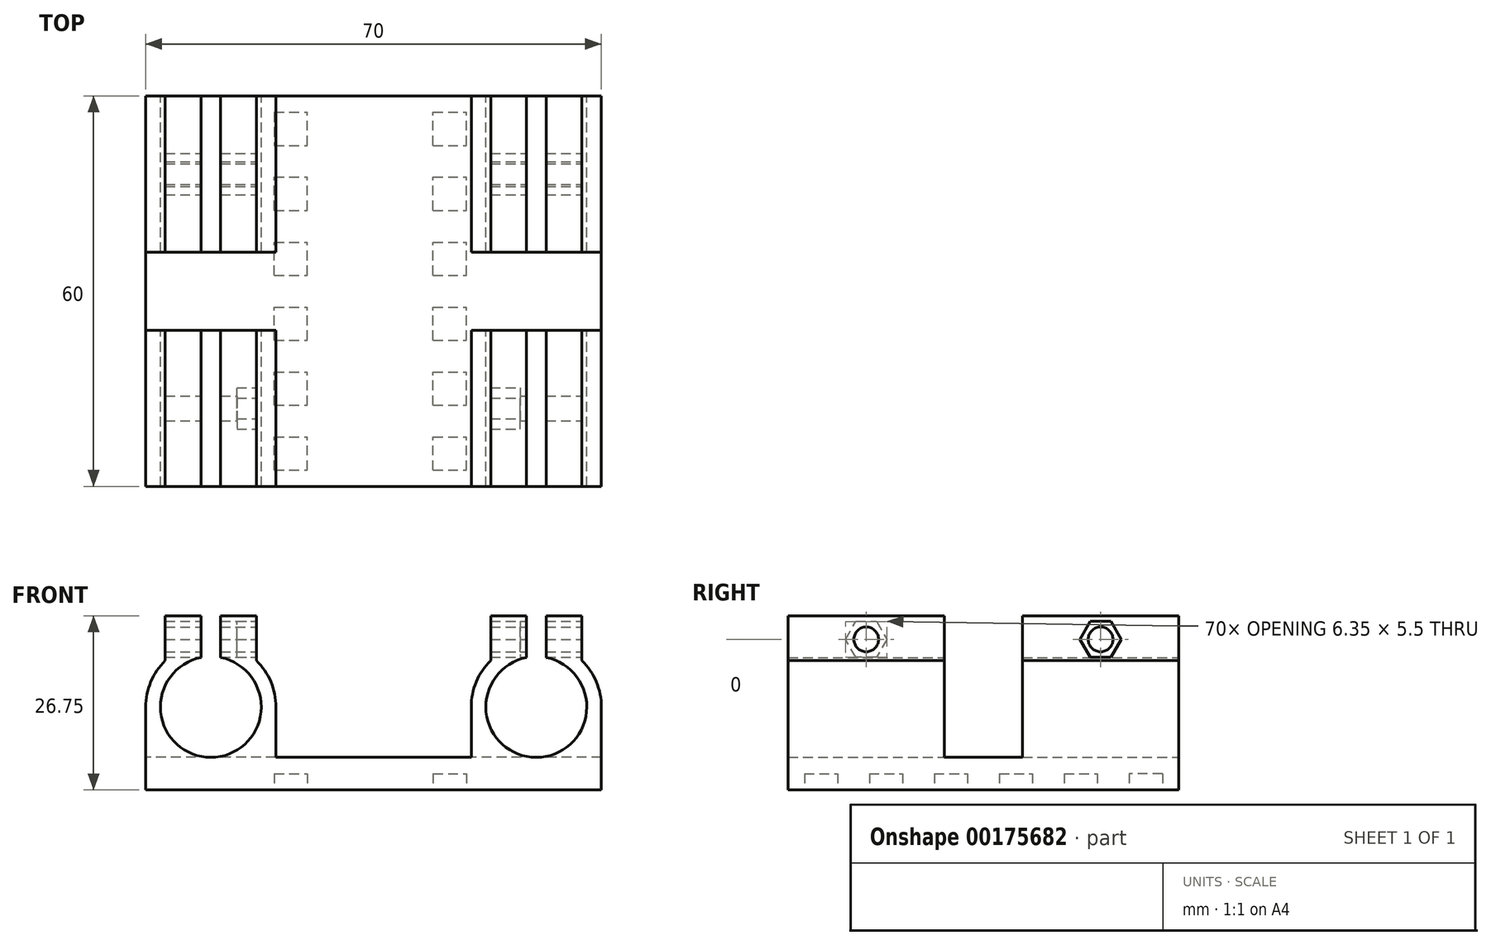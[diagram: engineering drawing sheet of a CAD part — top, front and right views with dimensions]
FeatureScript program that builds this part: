
annotation { "Feature Type Name" : "Feature", "Feature Type Description" : "" }
export const myFeature = defineFeature(function(context is Context, id is Id, definition is map)
    precondition{}
    {
        {
            var Q0;
            Q0=qCreatedBy(makeId("Front.planeOp"),FACE);
            var sketch = newSketch(context, id + "F0", { "sketchPlane" : qUnion([Q0])});
            skLineSegment(sketch, "E0", {"start": v(0, 0) * mm, "end": v(-35, 0) * mm});
            skLineSegment(sketch, "E1", {"start": v(-35, 0) * mm, "end": v(-35, 12.75) * mm});
            skLineSegment(sketch, "E2", {"start": v(-15, 12.75) * mm, "end": v(-15, 5) * mm});
            skLineSegment(sketch, "E3", {"start": v(-15, 5) * mm, "end": v(0, 5) * mm});
            skArc(sketch, "E4", {"start": v(-26.5, 20.35) * mm, "mid": v(-25, 5) * mm, "end": v(-23.5, 20.35) * mm});
            skArc(sketch, "E5", {"start": v(-15, 12.75) * mm, "mid": v(-15.78, 16.62) * mm, "end": v(-18, 19.9) * mm});
            skLineSegment(sketch, "E6", {"start": v(-32, 19.9) * mm, "end": v(-32, 26.75) * mm});
            skLineSegment(sketch, "E7", {"start": v(-32, 26.75) * mm, "end": v(-26.5, 26.75) * mm});
            skLineSegment(sketch, "E8", {"start": v(-18, 26.75) * mm, "end": v(-18, 19.9) * mm});
            skLineSegment(sketch, "E9", {"start": v(-25, 33.97) * mm, "end": v(-25, -14.1) * mm, "construction": true});
            skLineSegment(sketch, "E10", {"start": v(-26.5, 26.75) * mm, "end": v(-26.5, 20.35) * mm});
            skLineSegment(sketch, "E11", {"start": v(-23.5, 26.75) * mm, "end": v(-23.5, 20.35) * mm});
            skLineSegment(sketch, "E12.trimOffspring", {"start": v(-23.5, 26.75) * mm, "end": v(-18, 26.75) * mm});
            skArc(sketch, "E13.trimOffspring", {"start": v(-32, 19.9) * mm, "mid": v(-34.22, 16.62) * mm, "end": v(-35, 12.75) * mm});
            skLineSegment(sketch, "E14.MirrorCS", {"start": v(15, 5) * mm, "end": v(0, 5) * mm});
            skLineSegment(sketch, "E15.MirrorCS", {"start": v(0, 0) * mm, "end": v(35, 0) * mm});
            skLineSegment(sketch, "E16.MirrorCS", {"start": v(35, 0) * mm, "end": v(35, 12.75) * mm});
            skArc(sketch, "E17.MirrorCS", {"start": v(32, 19.9) * mm, "mid": v(34.22, 16.62) * mm, "end": v(35, 12.75) * mm});
            skLineSegment(sketch, "E18.MirrorCS", {"start": v(32, 19.9) * mm, "end": v(32, 26.75) * mm});
            skLineSegment(sketch, "E19.MirrorCS", {"start": v(32, 26.75) * mm, "end": v(26.5, 26.75) * mm});
            skLineSegment(sketch, "E20.MirrorCS", {"start": v(26.5, 26.75) * mm, "end": v(26.5, 20.35) * mm});
            skArc(sketch, "E21.MirrorCS", {"start": v(26.5, 20.35) * mm, "mid": v(25, 5) * mm, "end": v(23.5, 20.35) * mm});
            skLineSegment(sketch, "E22.MirrorCS", {"start": v(23.5, 26.75) * mm, "end": v(23.5, 20.35) * mm});
            skLineSegment(sketch, "E23.MirrorCS", {"start": v(23.5, 26.75) * mm, "end": v(18, 26.75) * mm});
            skLineSegment(sketch, "E24.MirrorCS", {"start": v(18, 26.75) * mm, "end": v(18, 19.9) * mm});
            skArc(sketch, "E25.MirrorCS", {"start": v(15, 12.75) * mm, "mid": v(15.78, 16.62) * mm, "end": v(18, 19.9) * mm});
            skLineSegment(sketch, "E26.MirrorCS", {"start": v(15, 12.75) * mm, "end": v(15, 5) * mm});
            skSolve(sketch);
        }
        {
            var Q0;
            Q0 = qSketchRegion(id + "F0", true);
            extrude(context, id + "F1", {"entities" : qUnion([Q0]), "endBound" : BoundingType.SYMMETRIC, "depth" : 60 * mm});
        }
        {
            var Q0;
            Q0=makeQuery(id+"F1.opExtrude","SWEPT_FACE",FACE,{"disambiguationData":[OSD([sQuery(id+"F0.wireOp",EDGE,"E26.MirrorCS")])]});
            var sketch = newSketch(context, id + "F2", { "sketchPlane" : qUnion([Q0])});
            skLineSegment(sketch, "E27.0", {"start": v(30, 26.75) * mm, "end": v(-30, 26.75) * mm});
            skLineSegment(sketch, "E28.bottom", {"start": v(-6, 5) * mm, "end": v(6, 5) * mm});
            skLineSegment(sketch, "E28.top", {"start": v(-6, 26.75) * mm, "end": v(6, 26.75) * mm});
            skLineSegment(sketch, "E28.left", {"start": v(-6, 5) * mm, "end": v(-6, 26.75) * mm});
            skLineSegment(sketch, "E28.right", {"start": v(6, 5) * mm, "end": v(6, 26.75) * mm});
            skSolve(sketch);
        }
        {
            var Q0;
            Q0 = qSketchRegion(id + "F2", true);
            extrude(context, id + "F3", {"entities" : qUnion([Q0]), "operationType" : NewBodyOperationType.REMOVE, "endBound" : BoundingType.THROUGH_ALL, "oppositeDirection" : true, "depth" : 25 * mm, "hasSecondDirection" : true, "secondDirectionBound" : SecondDirectionBoundingType.THROUGH_ALL, "secondDirectionOppositeDirection" : false, "secondDirectionDepth" : 25 * mm});
        }
        {
            var Q0;
            {var subQ1=sQuery(id+"F0.wireOp",EDGE,"E8");Q0=makeQuery(id+"F3.boolean.opBoolean","SPLIT",FACE,{"disambiguationData":[TD([makeQuery(id+"F3.opExtrude","SWEPT_FACE",FACE,{"disambiguationData":[OSD([sQuery(id+"F2.wireOp",EDGE,"E28.right")])]})])],"derivedFrom":makeQuery(id+"F1.opExtrude","SWEPT_FACE",FACE,{"disambiguationData":[OSD([subQ1])]})});}
            var sketch = newSketch(context, id + "F4", { "sketchPlane" : qUnion([Q0])});
            skCircle(sketch, "E29.cCircle", {"center": v(-18, 23.14) * mm, "radius": 2.75 * mm, "construction": true});
            skLineSegment(sketch, "E29.0", {"start": v(-14.82, 23.14) * mm, "end": v(-16.41, 20.4) * mm});
            skLineSegment(sketch, "E29.1", {"start": v(-16.41, 20.4) * mm, "end": v(-19.59, 20.4) * mm});
            skLineSegment(sketch, "E29.2", {"start": v(-19.59, 20.4) * mm, "end": v(-21.18, 23.14) * mm});
            skLineSegment(sketch, "E29.3", {"start": v(-21.18, 23.14) * mm, "end": v(-19.59, 25.9) * mm});
            skLineSegment(sketch, "E29.4", {"start": v(-19.59, 25.9) * mm, "end": v(-16.41, 25.9) * mm});
            skLineSegment(sketch, "E29.5", {"start": v(-16.41, 25.9) * mm, "end": v(-14.82, 23.14) * mm});
            skPoint(sketch, "E29.0.midPoint", {"position": v(-15.62, 21.77) * mm});
            skCircle(sketch, "E30.MirrorC", {"center": v(18, 23.14) * mm, "radius": 2.75 * mm, "construction": true});
            skLineSegment(sketch, "E31.MirrorCS", {"start": v(16.41, 25.9) * mm, "end": v(14.82, 23.14) * mm});
            skLineSegment(sketch, "E32.MirrorCS", {"start": v(19.59, 25.9) * mm, "end": v(16.41, 25.9) * mm});
            skLineSegment(sketch, "E33.MirrorCS", {"start": v(21.18, 23.14) * mm, "end": v(19.59, 25.9) * mm});
            skLineSegment(sketch, "E34.MirrorCS", {"start": v(19.59, 20.4) * mm, "end": v(21.18, 23.14) * mm});
            skLineSegment(sketch, "E35.MirrorCS", {"start": v(16.41, 20.4) * mm, "end": v(19.59, 20.4) * mm});
            skLineSegment(sketch, "E36.MirrorCS", {"start": v(14.82, 23.14) * mm, "end": v(16.41, 20.4) * mm});
            skCircle(sketch, "E37", {"center": v(-18, 23.14) * mm, "radius": 1.9 * mm});
            skCircle(sketch, "E38.MirrorC", {"center": v(18, 23.14) * mm, "radius": 1.9 * mm});
            skSolve(sketch);
        }
        {
            var Q0;
            Q0 = qSketchRegion(id + "F4", true);
            extrude(context, id + "F5", {"entities" : qUnion([Q0]), "operationType" : NewBodyOperationType.REMOVE, "oppositeDirection" : true, "depth" : 3 * mm, "hasSecondDirection" : true, "secondDirectionOppositeDirection" : false, "secondDirectionDepth" : 40.5 * mm});
        }
        {
            var Q0;
            Q0=makeQuery(id+"F4.imprint","IMPRINT",FACE,{"disambiguationData":[TD([[makeQuery(id+"F4.imprint","IMPRINT",EDGE,{"derivedFrom":sQuery(id+"F4.wireOp",EDGE,"E38.MirrorC")}),-1.0]])]});
            var Q1;
            Q1=makeQuery(id+"F4.imprint","IMPRINT",FACE,{"disambiguationData":[TD([[makeQuery(id+"F4.imprint","IMPRINT",EDGE,{"derivedFrom":sQuery(id+"F4.wireOp",EDGE,"E37")}),1.0]])]});
            extrude(context, id + "F6", {"entities" : qUnion([Q0, Q1]), "operationType" : NewBodyOperationType.REMOVE, "endBound" : BoundingType.THROUGH_ALL, "oppositeDirection" : true, "depth" : 25 * mm, "hasSecondDirection" : true, "secondDirectionBound" : SecondDirectionBoundingType.THROUGH_ALL, "secondDirectionOppositeDirection" : false, "secondDirectionDepth" : 25 * mm});
        }
        {
            var Q0;
            Q0=makeQuery(id+"F1.opExtrude","SWEPT_FACE",FACE,{"disambiguationData":[OSD([sQuery(id+"F0.wireOp",EDGE,"E0"),sQuery(id+"F0.wireOp",EDGE,"E15.MirrorCS")])]});
            var sketch = newSketch(context, id + "F7", { "sketchPlane" : qUnion([Q0])});
            skLineSegment(sketch, "E39.bottom", {"start": v(-15.25, 27.5) * mm, "end": v(-10.15, 27.5) * mm});
            skLineSegment(sketch, "E39.top", {"start": v(-15.25, 22.4) * mm, "end": v(-10.15, 22.4) * mm});
            skLineSegment(sketch, "E39.left", {"start": v(-15.25, 27.5) * mm, "end": v(-15.25, 22.4) * mm});
            skLineSegment(sketch, "E39.right", {"start": v(-10.15, 27.5) * mm, "end": v(-10.15, 22.4) * mm});
            skLineSegment(sketch, "E40.1.0.0", {"start": v(14.25, 27.5) * mm, "end": v(14.25, 22.4) * mm});
            skLineSegment(sketch, "E40.1.0.1", {"start": v(9.15, 27.5) * mm, "end": v(14.25, 27.5) * mm});
            skLineSegment(sketch, "E40.1.0.2", {"start": v(9.15, 27.5) * mm, "end": v(9.15, 22.4) * mm});
            skLineSegment(sketch, "E40.1.0.3", {"start": v(9.15, 22.4) * mm, "end": v(14.25, 22.4) * mm});
            skLineSegment(sketch, "E40.direction1", {"start": v(-10.15, 22.4) * mm, "end": v(14.25, 22.4) * mm, "construction": true});
            skLineSegment(sketch, "E41.1.0.0", {"start": v(-10.15, 17.52) * mm, "end": v(-10.15, 12.42) * mm});
            skLineSegment(sketch, "E41.1.0.1", {"start": v(-15.25, 17.52) * mm, "end": v(-15.25, 12.42) * mm});
            skLineSegment(sketch, "E41.1.0.2", {"start": v(-15.25, 12.42) * mm, "end": v(-10.15, 12.42) * mm});
            skLineSegment(sketch, "E41.1.0.3", {"start": v(-15.25, 17.52) * mm, "end": v(-10.15, 17.52) * mm});
            skLineSegment(sketch, "E41.1.0.4", {"start": v(9.15, 17.52) * mm, "end": v(14.25, 17.52) * mm});
            skLineSegment(sketch, "E41.1.0.5", {"start": v(9.15, 17.52) * mm, "end": v(9.15, 12.42) * mm});
            skLineSegment(sketch, "E41.1.0.6", {"start": v(14.25, 17.52) * mm, "end": v(14.25, 12.42) * mm});
            skLineSegment(sketch, "E41.1.0.7", {"start": v(-10.15, 12.42) * mm, "end": v(14.25, 12.42) * mm, "construction": true});
            skLineSegment(sketch, "E41.2.0.0", {"start": v(-10.15, 7.54) * mm, "end": v(-10.15, 2.44) * mm});
            skLineSegment(sketch, "E41.2.0.1", {"start": v(-15.25, 7.54) * mm, "end": v(-15.25, 2.44) * mm});
            skLineSegment(sketch, "E41.2.0.2", {"start": v(-15.25, 2.44) * mm, "end": v(-10.15, 2.44) * mm});
            skLineSegment(sketch, "E41.2.0.3", {"start": v(-15.25, 7.54) * mm, "end": v(-10.15, 7.54) * mm});
            skLineSegment(sketch, "E41.2.0.4", {"start": v(9.15, 7.54) * mm, "end": v(14.25, 7.54) * mm});
            skLineSegment(sketch, "E41.2.0.5", {"start": v(9.15, 7.54) * mm, "end": v(9.15, 2.44) * mm});
            skLineSegment(sketch, "E41.2.0.6", {"start": v(14.25, 7.54) * mm, "end": v(14.25, 2.44) * mm});
            skLineSegment(sketch, "E41.2.0.7", {"start": v(-10.15, 2.44) * mm, "end": v(14.25, 2.44) * mm, "construction": true});
            skLineSegment(sketch, "E41.direction1", {"start": v(-10.15, 22.4) * mm, "end": v(-10.15, 12.42) * mm, "construction": true});
            skLineSegment(sketch, "E42.0.3.0", {"start": v(-10.15, -2.44) * mm, "end": v(-10.15, -7.54) * mm});
            skLineSegment(sketch, "E42.3.3.0", {"start": v(-15.25, -2.44) * mm, "end": v(-15.25, -7.54) * mm});
            skLineSegment(sketch, "E42.6.3.0", {"start": v(-15.25, -7.54) * mm, "end": v(-10.15, -7.54) * mm});
            skLineSegment(sketch, "E42.9.3.0", {"start": v(-15.25, -2.44) * mm, "end": v(-10.15, -2.44) * mm});
            skLineSegment(sketch, "E42.12.3.0", {"start": v(9.15, -2.44) * mm, "end": v(14.25, -2.44) * mm});
            skLineSegment(sketch, "E42.15.3.0", {"start": v(9.15, -2.44) * mm, "end": v(9.15, -7.54) * mm});
            skLineSegment(sketch, "E42.18.3.0", {"start": v(14.25, -2.44) * mm, "end": v(14.25, -7.54) * mm});
            skLineSegment(sketch, "E42.21.3.0", {"start": v(-10.15, -7.54) * mm, "end": v(14.25, -7.54) * mm, "construction": true});
            skLineSegment(sketch, "E42.0.4.0", {"start": v(-10.15, -12.42) * mm, "end": v(-10.15, -17.52) * mm});
            skLineSegment(sketch, "E42.3.4.0", {"start": v(-15.25, -12.42) * mm, "end": v(-15.25, -17.52) * mm});
            skLineSegment(sketch, "E42.6.4.0", {"start": v(-15.25, -17.52) * mm, "end": v(-10.15, -17.52) * mm});
            skLineSegment(sketch, "E42.9.4.0", {"start": v(-15.25, -12.42) * mm, "end": v(-10.15, -12.42) * mm});
            skLineSegment(sketch, "E42.12.4.0", {"start": v(9.15, -12.42) * mm, "end": v(14.25, -12.42) * mm});
            skLineSegment(sketch, "E42.15.4.0", {"start": v(9.15, -12.42) * mm, "end": v(9.15, -17.52) * mm});
            skLineSegment(sketch, "E42.18.4.0", {"start": v(14.25, -12.42) * mm, "end": v(14.25, -17.52) * mm});
            skLineSegment(sketch, "E42.21.4.0", {"start": v(-10.15, -17.52) * mm, "end": v(14.25, -17.52) * mm, "construction": true});
            skLineSegment(sketch, "E42.0.5.0", {"start": v(-10.15, -22.4) * mm, "end": v(-10.15, -27.5) * mm});
            skLineSegment(sketch, "E42.3.5.0", {"start": v(-15.25, -27.5) * mm, "end": v(-15.25, -22.4) * mm});
            skLineSegment(sketch, "E42.6.5.0", {"start": v(-15.25, -27.5) * mm, "end": v(-10.15, -27.5) * mm});
            skLineSegment(sketch, "E42.9.5.0", {"start": v(-15.25, -22.4) * mm, "end": v(-10.15, -22.4) * mm});
            skLineSegment(sketch, "E42.12.5.0", {"start": v(9.15, -22.4) * mm, "end": v(14.25, -22.4) * mm});
            skLineSegment(sketch, "E42.15.5.0", {"start": v(9.15, -22.4) * mm, "end": v(9.15, -27.5) * mm});
            skLineSegment(sketch, "E42.18.5.0", {"start": v(14.25, -22.4) * mm, "end": v(14.25, -27.5) * mm});
            skLineSegment(sketch, "E42.21.5.0", {"start": v(-10.15, -27.5) * mm, "end": v(14.25, -27.5) * mm, "construction": true});
            skLineSegment(sketch, "E43", {"start": v(9.15, 12.42) * mm, "end": v(14.25, 12.42) * mm});
            skLineSegment(sketch, "E44", {"start": v(9.15, 2.44) * mm, "end": v(14.25, 2.44) * mm});
            skLineSegment(sketch, "E45", {"start": v(9.15, -7.54) * mm, "end": v(14.25, -7.54) * mm});
            skLineSegment(sketch, "E46", {"start": v(9.15, -17.52) * mm, "end": v(14.25, -17.52) * mm});
            skLineSegment(sketch, "E47", {"start": v(9.15, -27.5) * mm, "end": v(14.25, -27.5) * mm});
            skSolve(sketch);
        }
        {
            var Q0;
            Q0 = qSketchRegion(id + "F7", true);
            extrude(context, id + "F8", {"entities" : qUnion([Q0]), "operationType" : NewBodyOperationType.REMOVE, "oppositeDirection" : true, "depth" : 2.5 * mm});
        }
    });
